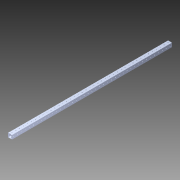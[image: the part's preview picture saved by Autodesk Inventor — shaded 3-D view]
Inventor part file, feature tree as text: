
AUTODESK INVENTOR PART (.ipt)
format: ipt  version: 2014 SP1 (Build 180222100, 222)  size: 1,657,856 bytes
history: native  units: in
note: dims shown in document units (in); Inventor stores cm internally (conversion verified against a paired STEP export)
features: extrude x2, sketch x2, pattern_circular x1, other x1, mirror x1, imported_body x1
ambient origin geometry x8: Origin, YZ Plane, XZ Plane, XY Plane, X Axis, Y Axis, Z Axis, Center Point
bodies: Body1 (feature_tree)
feature tree (8):
  pattern_circular  "CirPattern2"
  other  "1x1 tube1"
  extrude  "Extrusion1"  Depth=1.0in TaperAngle=0.0deg
  mirror  "Mirror1"
  extrude  "Extrusion2"  [1 undecoded]
  imported_body  "Base1"
  sketch  "Sketch1"  dims[d0=38.0in d1=0.0in d2=1.0in d3=0.0in]
  sketch  "Sketch3"
note: 1 required parameter value undecoded (feature->parameter linkage not recoverable at this tier; creation-order binding heuristic only, values carry confidence <= 0.55)
